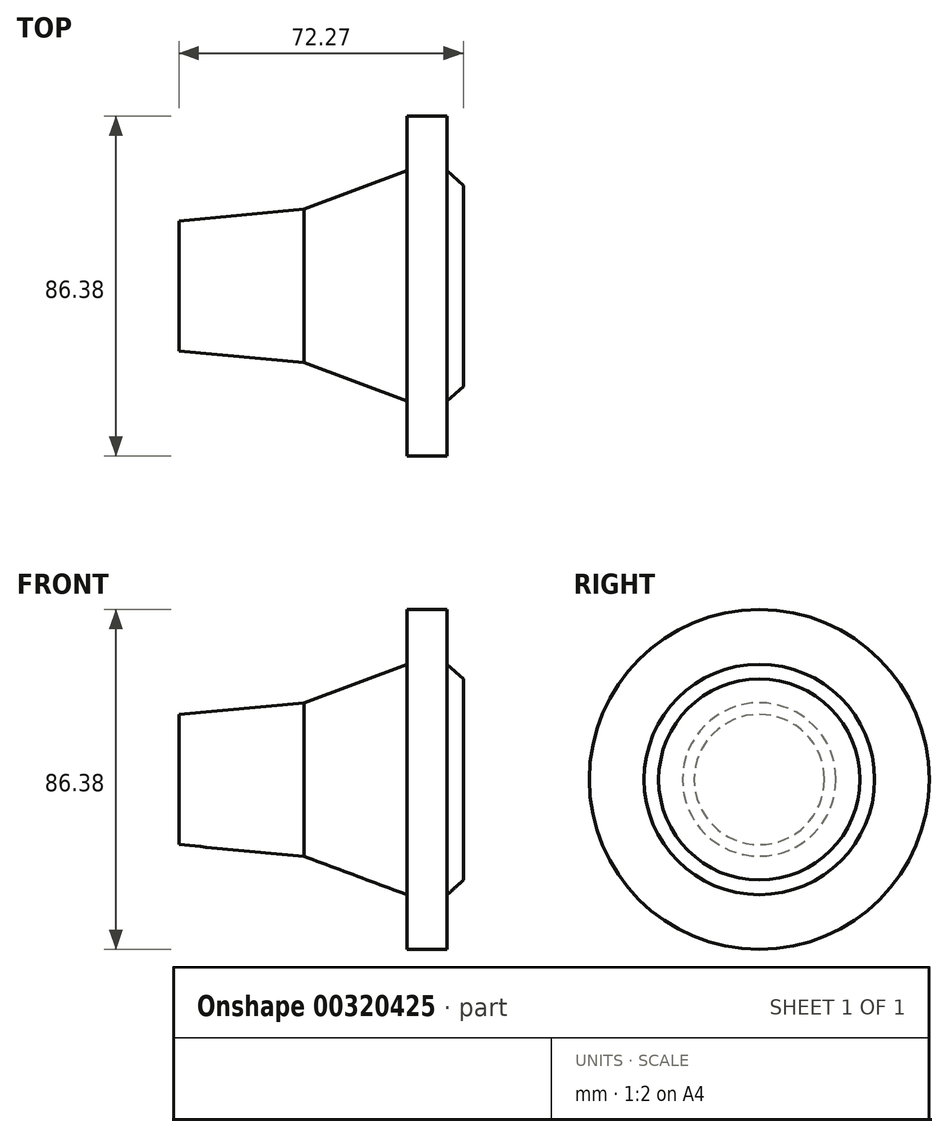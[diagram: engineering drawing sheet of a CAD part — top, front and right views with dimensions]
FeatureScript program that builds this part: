
annotation { "Feature Type Name" : "Feature", "Feature Type Description" : "" }
export const myFeature = defineFeature(function(context is Context, id is Id, definition is map)
    precondition{}
    {
        {
            var Q0;
            Q0=qCreatedBy(makeId("Front.planeOp"),FACE);
            var sketch = newSketch(context, id + "F0", { "sketchPlane" : qUnion([Q0])});
            skLineSegment(sketch, "E0", {"start": v(0, 0) * mm, "end": v(0, 16.55) * mm});
            skLineSegment(sketch, "E1", {"start": v(0, 16.55) * mm, "end": v(31.73, 19.49) * mm});
            skLineSegment(sketch, "E2", {"start": v(31.73, 19.49) * mm, "end": v(57.98, 29.28) * mm});
            skLineSegment(sketch, "E3", {"start": v(57.98, 29.28) * mm, "end": v(57.98, 43.19) * mm});
            skLineSegment(sketch, "E4", {"start": v(57.98, 43.19) * mm, "end": v(68.16, 43.19) * mm});
            skLineSegment(sketch, "E5", {"start": v(68.16, 43.19) * mm, "end": v(68.16, 29.28) * mm});
            skLineSegment(sketch, "E6", {"start": v(68.16, 29.28) * mm, "end": v(72.27, 25.56) * mm});
            skLineSegment(sketch, "E7", {"start": v(72.27, 25.56) * mm, "end": v(72.27, 0) * mm});
            skLineSegment(sketch, "E8", {"start": v(72.27, 0) * mm, "end": v(0, 0) * mm});
            skSolve(sketch);
        }
        {
            var Q0;
            Q0=makeQuery(id+"F0.imprint","IMPRINT",FACE,{"disambiguationData":[TD([[makeQuery(id+"F0.imprint","IMPRINT",EDGE,{"derivedFrom":sQuery(id+"F0.wireOp",EDGE,"E0")}),-1.0]])]});
            var Q1;
            Q1=sQuery(id+"F0.wireOp",EDGE,"E8");
            revolve(context, id + "F1", {"entities" : qUnion([Q0]), "axis" : qUnion([Q1]), "revolveType" : RevolveType.FULL});
        }
    });
